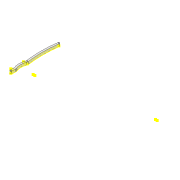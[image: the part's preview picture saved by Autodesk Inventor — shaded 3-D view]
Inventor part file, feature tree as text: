
AUTODESK INVENTOR PART (.ipt)
format: ipt  version: 2022 (Build 260153000, 153)  size: 134,144 bytes
history: native  units: mm
features: sketch x2, extrude x1, fillet x1, projected_geometry x1
ambient origin geometry x8: Origin, YZ Plane, XZ Plane, XY Plane, X Axis, Y Axis, Z Axis, Center Point
bodies: Solid1 (feature_tree)
feature tree (5):
  extrude  "Extrusion1"  Depth=6.0mm
  fillet  "Fillet1"  Radius=3.0mm
  sketch  "Sketch2"  dims[d3=3.0mm d4=8.0mm d5=0.0mm d10=3.0mm d11=57.227mm d12=400.0mm d13=400.0mm d16=15.0mm d17=55.0mm d18=50.0mm d19=50.0mm d20=10.0mm]
  sketch  "Sketch1"  dims[d0=167.039mm d1=6.0mm d2=3.0mm]
  projected_geometry  "Projected Loop1"
